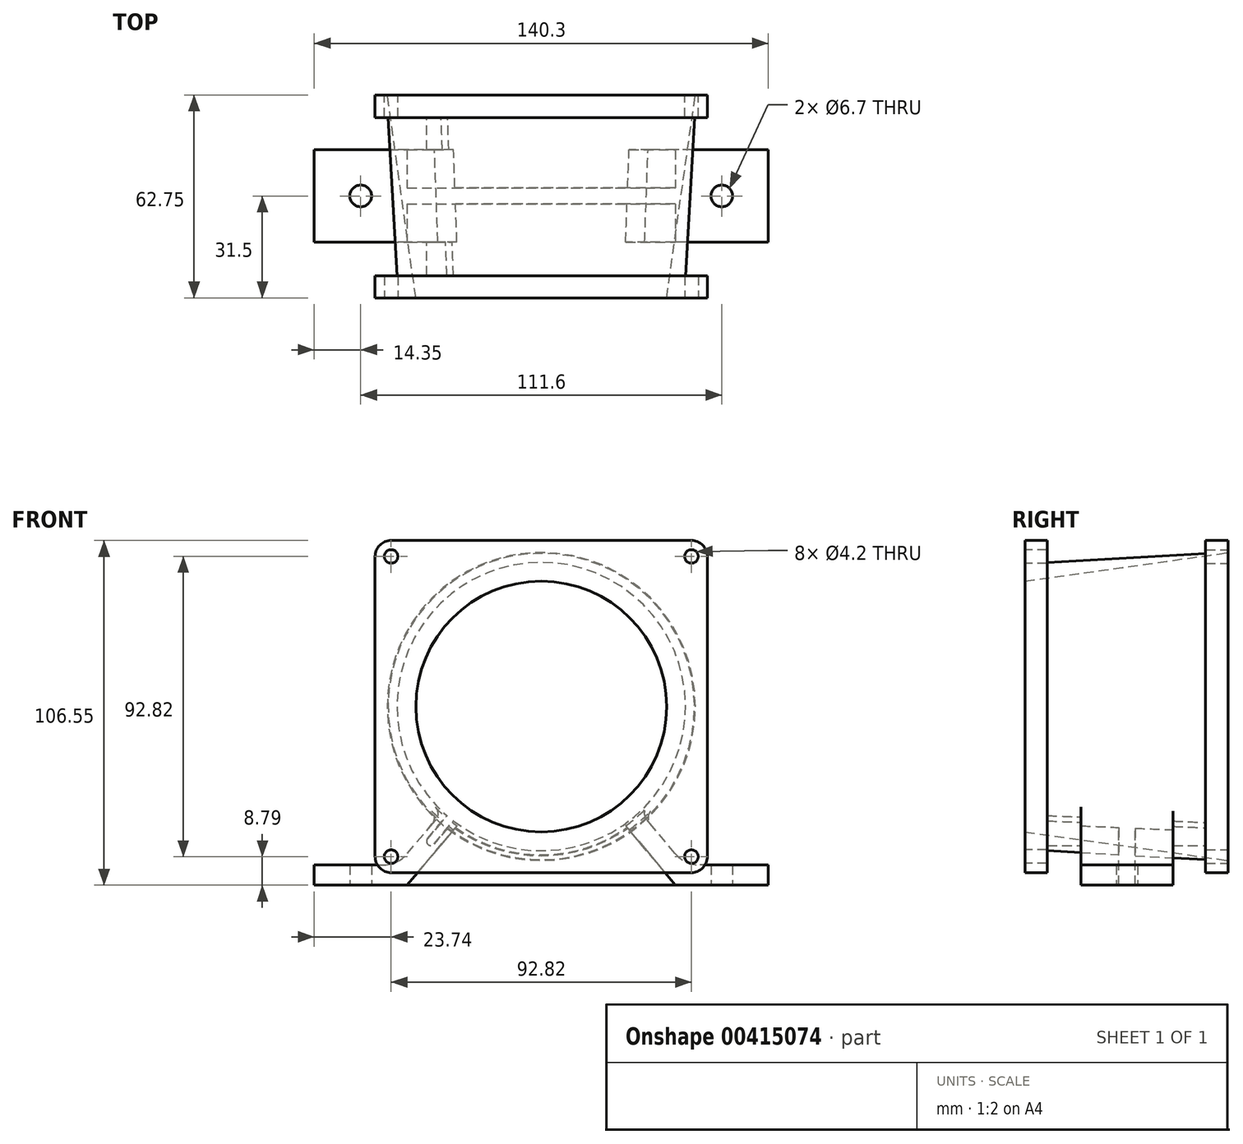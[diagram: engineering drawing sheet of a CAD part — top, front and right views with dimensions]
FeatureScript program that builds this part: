
annotation { "Feature Type Name" : "Feature", "Feature Type Description" : "" }
export const myFeature = defineFeature(function(context is Context, id is Id, definition is map)
    precondition{}
    {
        {
            var Q0;
            Q0=qCreatedBy(makeId("Front.planeOp"),FACE);
            var sketch = newSketch(context, id + "F0", { "sketchPlane" : qUnion([Q0])});
            skLineSegment(sketch, "E0.bottom", {"start": v(-51.35, 51.35) * mm, "end": v(51.35, 51.35) * mm});
            skLineSegment(sketch, "E0.top", {"start": v(-51.35, -51.35) * mm, "end": v(51.35, -51.35) * mm});
            skLineSegment(sketch, "E0.left", {"start": v(-51.35, 51.35) * mm, "end": v(-51.35, -51.35) * mm});
            skLineSegment(sketch, "E0.right", {"start": v(51.35, 51.35) * mm, "end": v(51.35, -51.35) * mm});
            skPoint(sketch, "E0.middle", {"position": v(0, 0) * mm});
            skCircle(sketch, "E1", {"center": v(46.4, 46.41) * mm, "radius": 2.1 * mm});
            skLineSegment(sketch, "E2", {"start": v(0, 51.35) * mm, "end": v(0, -51.35) * mm, "construction": true});
            skLineSegment(sketch, "E3", {"start": v(-51.35, 0) * mm, "end": v(51.35, 0) * mm, "construction": true});
            skCircle(sketch, "E4.MirrorC", {"center": v(-46.4, 46.41) * mm, "radius": 2.1 * mm});
            skCircle(sketch, "E5.MirrorC", {"center": v(-46.4, -46.41) * mm, "radius": 2.1 * mm});
            skCircle(sketch, "E6.MirrorC", {"center": v(46.4, -46.41) * mm, "radius": 2.1 * mm});
            skSolve(sketch);
        }
        {
            var Q0;
            Q0=makeQuery(id+"F0.imprint","IMPRINT",FACE,{"disambiguationData":[TD([[makeQuery(id+"F0.imprint","IMPRINT",EDGE,{"derivedFrom":sQuery(id+"F0.wireOp",EDGE,"E0.bottom")}),-1.0]])]});
            extrude(context, id + "F1", {"entities" : qUnion([Q0]), "oppositeDirection" : true, "depth" : 6.85 * mm});
        }
        {
            var Q0;
            Q0=makeQuery(id+"F1.opExtrude","SWEPT_EDGE",EDGE,{"disambiguationData":[OSD([sQuery(id+"F0.wireOp",EDGE,"E0.bottom"),sQuery(id+"F0.wireOp",EDGE,"E0.left")])]});
            var Q1;
            Q1=makeQuery(id+"F1.opExtrude","SWEPT_EDGE",EDGE,{"disambiguationData":[OSD([sQuery(id+"F0.wireOp",EDGE,"E0.bottom"),sQuery(id+"F0.wireOp",EDGE,"E0.right")])]});
            var Q2;
            Q2=makeQuery(id+"F1.opExtrude","SWEPT_EDGE",EDGE,{"disambiguationData":[OSD([sQuery(id+"F0.wireOp",EDGE,"E0.top"),sQuery(id+"F0.wireOp",EDGE,"E0.right")])]});
            var Q3;
            Q3=makeQuery(id+"F1.opExtrude","SWEPT_EDGE",EDGE,{"disambiguationData":[OSD([sQuery(id+"F0.wireOp",EDGE,"E0.top"),sQuery(id+"F0.wireOp",EDGE,"E0.left")])]});
            fillet(context, id + "F2", {"entities" : qUnion([Q0, Q1, Q2, Q3]), "radius" : 5 * mm, "tangentPropagation" : true, "allowEdgeOverflow" : false});
        }
        {
            var Q0;
            Q0=makeQuery(id+"F1.opExtrude","CAP_FACE",FACE,{"disambiguationData":[OSD([sQuery(id+"F0.wireOp",EDGE,"E0.bottom"),sQuery(id+"F0.wireOp",EDGE,"E0.top"),sQuery(id+"F0.wireOp",EDGE,"E0.left"),sQuery(id+"F0.wireOp",EDGE,"E0.right"),sQuery(id+"F0.wireOp",EDGE,"E1"),sQuery(id+"F0.wireOp",EDGE,"E4.MirrorC"),sQuery(id+"F0.wireOp",EDGE,"E5.MirrorC"),sQuery(id+"F0.wireOp",EDGE,"E6.MirrorC")])],"isStart":false});
            cPlane(context, id + "F3", {"entities" : qUnion([Q0]), "cplaneType" : CPlaneType.OFFSET, "offset" : 55.9 * mm, "width" : 150 * mm, "height" : 150 * mm});
        }
        {
            var Q0;
            Q0=qCreatedBy(id+"F3.planeOp",FACE);
            var sketch = newSketch(context, id + "F4", { "sketchPlane" : qUnion([Q0])});
            skLineSegment(sketch, "E7.bottom", {"start": v(-51.35, 51.35) * mm, "end": v(51.35, 51.35) * mm});
            skLineSegment(sketch, "E7.top", {"start": v(-51.35, -51.35) * mm, "end": v(51.35, -51.35) * mm});
            skLineSegment(sketch, "E7.left", {"start": v(-51.35, 51.35) * mm, "end": v(-51.35, -51.35) * mm});
            skLineSegment(sketch, "E7.right", {"start": v(51.35, 51.35) * mm, "end": v(51.35, -51.35) * mm});
            skPoint(sketch, "E7.middle", {"position": v(0, 0) * mm});
            skCircle(sketch, "E8.0", {"center": v(-46.4, 46.41) * mm, "radius": 2.1 * mm});
            skCircle(sketch, "E9.0", {"center": v(46.4, 46.41) * mm, "radius": 2.1 * mm});
            skCircle(sketch, "E10.0", {"center": v(46.4, -46.41) * mm, "radius": 2.1 * mm});
            skCircle(sketch, "E11.0", {"center": v(-46.4, -46.41) * mm, "radius": 2.1 * mm});
            skSolve(sketch);
        }
        {
            var Q0;
            Q0=makeQuery(id+"F4.imprint","IMPRINT",FACE,{"disambiguationData":[TD([[makeQuery(id+"F4.imprint","IMPRINT",EDGE,{"derivedFrom":sQuery(id+"F4.wireOp",EDGE,"E7.bottom")}),-1.0]])]});
            extrude(context, id + "F5", {"entities" : qUnion([Q0]), "oppositeDirection" : true, "depth" : 7 * mm});
        }
        {
            var Q0;
            Q0=makeQuery(id+"F5.opExtrude","SWEPT_EDGE",EDGE,{"disambiguationData":[OSD([sQuery(id+"F4.wireOp",EDGE,"E7.bottom"),sQuery(id+"F4.wireOp",EDGE,"E7.left")])]});
            var Q1;
            Q1=makeQuery(id+"F5.opExtrude","SWEPT_EDGE",EDGE,{"disambiguationData":[OSD([sQuery(id+"F4.wireOp",EDGE,"E7.bottom"),sQuery(id+"F4.wireOp",EDGE,"E7.right")])]});
            var Q2;
            Q2=makeQuery(id+"F5.opExtrude","SWEPT_EDGE",EDGE,{"disambiguationData":[OSD([sQuery(id+"F4.wireOp",EDGE,"E7.top"),sQuery(id+"F4.wireOp",EDGE,"E7.right")])]});
            var Q3;
            Q3=makeQuery(id+"F5.opExtrude","SWEPT_EDGE",EDGE,{"disambiguationData":[OSD([sQuery(id+"F4.wireOp",EDGE,"E7.top"),sQuery(id+"F4.wireOp",EDGE,"E7.left")])]});
            fillet(context, id + "F6", {"entities" : qUnion([Q0, Q1, Q2, Q3]), "radius" : 5 * mm, "tangentPropagation" : true, "allowEdgeOverflow" : false});
        }
        {
            var Q0;
            Q0=makeQuery(id+"F1.opExtrude","CAP_FACE",FACE,{"disambiguationData":[OSD([sQuery(id+"F0.wireOp",EDGE,"E0.bottom"),sQuery(id+"F0.wireOp",EDGE,"E0.top"),sQuery(id+"F0.wireOp",EDGE,"E0.left"),sQuery(id+"F0.wireOp",EDGE,"E0.right"),sQuery(id+"F0.wireOp",EDGE,"E1"),sQuery(id+"F0.wireOp",EDGE,"E4.MirrorC"),sQuery(id+"F0.wireOp",EDGE,"E5.MirrorC"),sQuery(id+"F0.wireOp",EDGE,"E6.MirrorC")])],"isStart":true});
            var sketch = newSketch(context, id + "F7", { "sketchPlane" : qUnion([Q0])});
            skCircle(sketch, "E12.0", {"center": v(0, 0) * mm, "radius": 44.18 * mm});
            skSolve(sketch);
        }
        {
            var Q0;
            Q0=makeQuery(id+"F5.opExtrude","CAP_FACE",FACE,{"disambiguationData":[OSD([sQuery(id+"F4.wireOp",EDGE,"E7.bottom"),sQuery(id+"F4.wireOp",EDGE,"E7.top"),sQuery(id+"F4.wireOp",EDGE,"E7.left"),sQuery(id+"F4.wireOp",EDGE,"E7.right"),sQuery(id+"F4.wireOp",EDGE,"E8.0"),sQuery(id+"F4.wireOp",EDGE,"E9.0"),sQuery(id+"F4.wireOp",EDGE,"E10.0"),sQuery(id+"F4.wireOp",EDGE,"E11.0")])],"isStart":true});
            var sketch = newSketch(context, id + "F8", { "sketchPlane" : qUnion([Q0])});
            skCircle(sketch, "E13.0", {"center": v(0, 0) * mm, "radius": 47.75 * mm});
            skSolve(sketch);
        }
        {
            var Q0;
            Q0=makeQuery(id+"F7.imprint","IMPRINT",FACE,{"disambiguationData":[TD([[makeQuery(id+"F7.imprint","IMPRINT",EDGE,{"derivedFrom":sQuery(id+"F7.wireOp",EDGE,"E12.0")}),1.0]])]});
            var Q1;
            Q1=makeQuery(id+"F8.imprint","IMPRINT",FACE,{"disambiguationData":[TD([[makeQuery(id+"F8.imprint","IMPRINT",EDGE,{"derivedFrom":sQuery(id+"F8.wireOp",EDGE,"E13.0")}),1.0]])]});
            loft(context, id + "F9", {"operationType" : NewBodyOperationType.ADD, "sheetProfilesArray" : [{ "sheetProfileEntities" : qUnion([Q0]) }, { "sheetProfileEntities" : qUnion([Q1]) }]});
        }
        {
            var Q0;
            Q0=makeQuery(id+"F7.imprint","IMPRINT",FACE,{"disambiguationData":[TD([[makeQuery(id+"F7.imprint","IMPRINT",EDGE,{"derivedFrom":sQuery(id+"F7.wireOp",EDGE,"E12.0")}),1.0]])]});
            var sketch = newSketch(context, id + "F10", { "sketchPlane" : qUnion([Q0])});
            skCircle(sketch, "E14.0", {"center": v(0, 0) * mm, "radius": 44.18 * mm});
            skCircle(sketch, "E15.0", {"center": v(0, 0) * mm, "radius": 38.75 * mm});
            skSolve(sketch);
        }
        {
            var Q0;
            Q0=makeQuery(id+"F8.imprint","IMPRINT",FACE,{"disambiguationData":[TD([[makeQuery(id+"F8.imprint","IMPRINT",EDGE,{"derivedFrom":sQuery(id+"F8.wireOp",EDGE,"E13.0")}),1.0]])]});
            var sketch = newSketch(context, id + "F11", { "sketchPlane" : qUnion([Q0])});
            skCircle(sketch, "E16.0", {"center": v(0, 0) * mm, "radius": 47.75 * mm});
            skCircle(sketch, "E17.0", {"center": v(0, 0) * mm, "radius": 47.6 * mm});
            skSolve(sketch);
        }
        {
            var Q0;
            Q0=makeQuery(id+"F1.opExtrude","CAP_FACE",FACE,{"disambiguationData":[OSD([sQuery(id+"F0.wireOp",EDGE,"E0.bottom"),sQuery(id+"F0.wireOp",EDGE,"E0.top"),sQuery(id+"F0.wireOp",EDGE,"E0.left"),sQuery(id+"F0.wireOp",EDGE,"E0.right"),sQuery(id+"F0.wireOp",EDGE,"E1"),sQuery(id+"F0.wireOp",EDGE,"E4.MirrorC"),sQuery(id+"F0.wireOp",EDGE,"E5.MirrorC"),sQuery(id+"F0.wireOp",EDGE,"E6.MirrorC")])],"isStart":false});
            cPlane(context, id + "F12", {"entities" : qUnion([Q0]), "cplaneType" : CPlaneType.OFFSET, "offset" : 10.4 * mm, "width" : 150 * mm, "height" : 150 * mm});
        }
        {
            var Q0;
            Q0=qCreatedBy(id+"F12.planeOp",FACE);
            var sketch = newSketch(context, id + "F13", { "sketchPlane" : qUnion([Q0])});
            skLineSegment(sketch, "E18.0", {"start": v(46.35, -51.35) * mm, "end": v(-46.35, -51.35) * mm, "construction": true});
            skLineSegment(sketch, "E19.0", {"start": v(34.1, -55.2) * mm, "end": v(-47.5, -55.2) * mm, "construction": true});
            skLineSegment(sketch, "E20.0", {"start": v(-51.35, 46.35) * mm, "end": v(-51.35, -46.35) * mm, "construction": true});
            skLineSegment(sketch, "E21", {"start": v(-51.35, -46.35) * mm, "end": v(-51.35, -55.2) * mm, "construction": true});
            skLineSegment(sketch, "E22", {"start": v(-51.35, -55.2) * mm, "end": v(-47.5, -55.2) * mm, "construction": true});
            skLineSegment(sketch, "E23.0", {"start": v(-70.15, -40.95) * mm, "end": v(-70.15, -55.2) * mm, "construction": true});
            skLineSegment(sketch, "E24", {"start": v(-70.15, -55.2) * mm, "end": v(-41.45, -55.2) * mm});
            skLineSegment(sketch, "E25", {"start": v(-70.15, -55.2) * mm, "end": v(-70.15, -49) * mm});
            skLineSegment(sketch, "E26", {"start": v(-70.15, -49) * mm, "end": v(-44.34, -49) * mm});
            skLineSegment(sketch, "E27", {"start": v(-44.34, -49) * mm, "end": v(-23.82, -24.54) * mm});
            skLineSegment(sketch, "E28", {"start": v(-23.82, -24.54) * mm, "end": v(-19.07, -28.52) * mm});
            skLineSegment(sketch, "E29", {"start": v(-19.07, -28.52) * mm, "end": v(-41.45, -55.2) * mm});
            skLineSegment(sketch, "E30.MirrorCS", {"start": v(23.82, -24.54) * mm, "end": v(19.07, -28.52) * mm});
            skLineSegment(sketch, "E31.MirrorCS", {"start": v(44.34, -49) * mm, "end": v(23.82, -24.54) * mm});
            skLineSegment(sketch, "E32.MirrorCS", {"start": v(19.07, -28.52) * mm, "end": v(41.45, -55.2) * mm});
            skLineSegment(sketch, "E33.MirrorCS", {"start": v(70.15, -55.2) * mm, "end": v(41.45, -55.2) * mm});
            skLineSegment(sketch, "E34.MirrorCS", {"start": v(70.15, -49) * mm, "end": v(44.34, -49) * mm});
            skLineSegment(sketch, "E35.MirrorCS", {"start": v(70.15, -55.2) * mm, "end": v(70.15, -49) * mm});
            skSolve(sketch);
        }
        {
            var Q0;
            Q0=makeQuery(id+"F13.imprint","IMPRINT",FACE,{"disambiguationData":[TD([[makeQuery(id+"F13.imprint","IMPRINT",EDGE,{"derivedFrom":sQuery(id+"F13.wireOp",EDGE,"E30.MirrorCS")}),1.0]])]});
            var Q1;
            Q1=makeQuery(id+"F13.imprint","IMPRINT",FACE,{"disambiguationData":[TD([[makeQuery(id+"F13.imprint","IMPRINT",EDGE,{"derivedFrom":sQuery(id+"F13.wireOp",EDGE,"E24")}),1.0]])]});
            extrude(context, id + "F14", {"entities" : qUnion([Q0, Q1]), "operationType" : NewBodyOperationType.ADD, "depth" : 28.5 * mm});
        }
        {
            var Q0;
            Q0=makeQuery(id+"F14.opExtrude","CAP_FACE",FACE,{"disambiguationData":[OSD([sQuery(id+"F13.wireOp",EDGE,"E30.MirrorCS"),sQuery(id+"F13.wireOp",EDGE,"E31.MirrorCS"),sQuery(id+"F13.wireOp",EDGE,"E32.MirrorCS"),sQuery(id+"F13.wireOp",EDGE,"E33.MirrorCS"),sQuery(id+"F13.wireOp",EDGE,"E34.MirrorCS"),sQuery(id+"F13.wireOp",EDGE,"E35.MirrorCS")])],"isStart":true});
            var sketch = newSketch(context, id + "F15", { "sketchPlane" : qUnion([Q0])});
            skLineSegment(sketch, "E36.0", {"start": v(-44.34, -49) * mm, "end": v(-30.88, -32.96) * mm, "construction": true});
            skLineSegment(sketch, "E37.0", {"start": v(-26.07, -36.87) * mm, "end": v(-41.45, -55.2) * mm, "construction": true});
            skLineSegment(sketch, "E38", {"start": v(-37.6, -40.98) * mm, "end": v(-32.86, -44.96) * mm, "construction": true});
            skLineSegment(sketch, "E39", {"start": v(-28.54, -35) * mm, "end": v(-34.14, -41.66) * mm, "construction": true});
            skArc(sketch, "E40", {"start": v(-35.13, -40.83) * mm, "mid": v(-34.97, -42.66) * mm, "end": v(-33.14, -42.5) * mm});
            skLineSegment(sketch, "E41", {"start": v(-35.13, -40.83) * mm, "end": v(-24.59, -28.26) * mm});
            skLineSegment(sketch, "E42", {"start": v(-33.14, -42.5) * mm, "end": v(-22.6, -29.93) * mm});
            skLineSegment(sketch, "E43", {"start": v(-22.6, -29.93) * mm, "end": v(-24.59, -28.26) * mm});
            skArc(sketch, "E44.MirrorCS", {"start": v(35.13, -40.83) * mm, "mid": v(34.97, -42.66) * mm, "end": v(33.14, -42.5) * mm});
            skLineSegment(sketch, "E45.MirrorCS", {"start": v(22.6, -29.93) * mm, "end": v(24.59, -28.26) * mm});
            skLineSegment(sketch, "E46.MirrorCS", {"start": v(33.14, -42.5) * mm, "end": v(22.6, -29.93) * mm});
            skLineSegment(sketch, "E47.MirrorCS", {"start": v(35.13, -40.83) * mm, "end": v(24.59, -28.26) * mm});
            skSolve(sketch);
        }
        {
            var Q0;
            {var subQ0=sQuery(id+"F15.wireOp",EDGE,"E40");Q0=makeQuery(id+"F15.imprint","IMPRINT",FACE,{"disambiguationData":[TD([[makeQuery(id+"F15.imprint","IMPRINT",EDGE,{"derivedFrom":subQ0}),1.0]])]});}
            var Q1;
            {var subQ0=sQuery(id+"F15.wireOp",EDGE,"E43");Q1=makeQuery(id+"F15.imprint","IMPRINT",FACE,{"disambiguationData":[TD([[makeQuery(id+"F15.imprint","IMPRINT",EDGE,{"derivedFrom":subQ0}),1.0]])]});}
            var Q2;
            Q2=makeQuery(id+"F15.imprint","IMPRINT",FACE,{"disambiguationData":[TD([[makeQuery(id+"F15.imprint","IMPRINT",EDGE,{"derivedFrom":sQuery(id+"F15.wireOp",EDGE,"E44.MirrorCS")}),-1.0]])]});
            var Q3;
            Q3=makeQuery(id+"F1.opExtrude","CAP_FACE",FACE,{"disambiguationData":[OSD([sQuery(id+"F0.wireOp",EDGE,"E0.bottom"),sQuery(id+"F0.wireOp",EDGE,"E0.top"),sQuery(id+"F0.wireOp",EDGE,"E0.left"),sQuery(id+"F0.wireOp",EDGE,"E0.right"),sQuery(id+"F0.wireOp",EDGE,"E1"),sQuery(id+"F0.wireOp",EDGE,"E4.MirrorC"),sQuery(id+"F0.wireOp",EDGE,"E5.MirrorC"),sQuery(id+"F0.wireOp",EDGE,"E6.MirrorC")])],"isStart":false});
            var Q4;
            Q4=makeQuery(id+"F5.opExtrude","CAP_FACE",FACE,{"disambiguationData":[OSD([sQuery(id+"F4.wireOp",EDGE,"E7.bottom"),sQuery(id+"F4.wireOp",EDGE,"E7.top"),sQuery(id+"F4.wireOp",EDGE,"E7.left"),sQuery(id+"F4.wireOp",EDGE,"E7.right"),sQuery(id+"F4.wireOp",EDGE,"E8.0"),sQuery(id+"F4.wireOp",EDGE,"E9.0"),sQuery(id+"F4.wireOp",EDGE,"E10.0"),sQuery(id+"F4.wireOp",EDGE,"E11.0")])],"isStart":false});
            extrude(context, id + "F16", {"entities" : qUnion([Q0, Q1, Q2]), "operationType" : NewBodyOperationType.ADD, "endBound" : BoundingType.UP_TO_SURFACE, "endBoundEntityFace" : qUnion([Q3]), "depth" : 25 * mm, "hasSecondDirection" : true, "secondDirectionBound" : SecondDirectionBoundingType.UP_TO_SURFACE, "secondDirectionOppositeDirection" : true, "secondDirectionBoundEntityFace" : qUnion([Q4]), "secondDirectionDepth" : 25 * mm});
        }
        {
            var Q1;
            Q1=makeQuery(id+"F10.imprint","IMPRINT",FACE,{"disambiguationData":[TD([[makeQuery(id+"F10.imprint","IMPRINT",EDGE,{"derivedFrom":sQuery(id+"F10.wireOp",EDGE,"E15.0")}),1.0]])]});
            var Q2;
            Q2=makeQuery(id+"F11.imprint","IMPRINT",FACE,{"disambiguationData":[TD([[makeQuery(id+"F11.imprint","IMPRINT",EDGE,{"derivedFrom":sQuery(id+"F11.wireOp",EDGE,"E17.0")}),1.0]])]});
            loft(context, id + "F17", {"operationType" : NewBodyOperationType.REMOVE, "sheetProfilesArray" : [{ "sheetProfileEntities" : qUnion([Q1]) }, { "sheetProfileEntities" : qUnion([Q2]) }]});
        }
        {
            var Q0;
            Q0=makeQuery(id+"F14.opExtrude","SWEPT_FACE",FACE,{"disambiguationData":[OSD([sQuery(id+"F13.wireOp",EDGE,"E33.MirrorCS")])]});
            var sketch = newSketch(context, id + "F18", { "sketchPlane" : qUnion([Q0])});
            skLineSegment(sketch, "E48", {"start": v(-41.45, -31.5) * mm, "end": v(30.35, -31.5) * mm, "construction": true});
            skLineSegment(sketch, "E49.0", {"start": v(-41.45, -34) * mm, "end": v(30.35, -34) * mm});
            skLineSegment(sketch, "E50.0", {"start": v(-41.45, -29) * mm, "end": v(30.35, -29) * mm});
            skLineSegment(sketch, "E51", {"start": v(-41.45, -29) * mm, "end": v(-41.45, -34) * mm});
            skLineSegment(sketch, "E52.0", {"start": v(41.45, -34) * mm, "end": v(41.45, -29) * mm});
            skLineSegment(sketch, "E53", {"start": v(30.35, -29) * mm, "end": v(41.45, -29) * mm});
            skLineSegment(sketch, "E54", {"start": v(30.35, -34) * mm, "end": v(41.45, -34) * mm});
            skSolve(sketch);
        }
        {
            var Q0;
            Q0=makeQuery(id+"F18.imprint","IMPRINT",FACE,{"disambiguationData":[TD([[makeQuery(id+"F18.imprint","IMPRINT",EDGE,{"derivedFrom":sQuery(id+"F18.wireOp",EDGE,"E49.0")}),1.0]])]});
            var Q1;
            {var subQ0=sQuery(id+"F13.wireOp",EDGE,"E29");Q1=makeQuery(id+"F16.boolean.opBoolean","SPLIT",FACE,{"disambiguationData":[TD([makeQuery(id+"F14.opExtrude","SWEPT_FACE",FACE,{"disambiguationData":[OSD([subQ0])]})])],"derivedFrom":makeQuery(id+"F9.opLoft","SWEPT_FACE",FACE,{"disambiguationData":[OSD([sQuery(id+"F7.wireOp",EDGE,"E12.0"),sQuery(id+"F8.wireOp",EDGE,"E13.0")])]})});}
            var Q2;
            Q2=makeQuery(id+"F1.opExtrude","SWEPT_BODY",BODY,{"disambiguationData":[OSD([sQuery(id+"F0.wireOp",EDGE,"E0.bottom"),sQuery(id+"F0.wireOp",EDGE,"E0.top"),sQuery(id+"F0.wireOp",EDGE,"E0.left"),sQuery(id+"F0.wireOp",EDGE,"E0.right"),sQuery(id+"F0.wireOp",EDGE,"E1"),sQuery(id+"F0.wireOp",EDGE,"E4.MirrorC"),sQuery(id+"F0.wireOp",EDGE,"E5.MirrorC"),sQuery(id+"F0.wireOp",EDGE,"E6.MirrorC")])]});
            extrude(context, id + "F19", {"entities" : qUnion([Q0]), "operationType" : NewBodyOperationType.ADD, "endBound" : BoundingType.UP_TO_BODY, "oppositeDirection" : true, "endBoundEntityFace" : qUnion([Q1]), "endBoundEntityBody" : qUnion([Q2]), "depth" : 25 * mm});
        }
        {
            var Q0;
            Q0=makeQuery(id+"F19.boolean.opBoolean","MERGE",FACE,{"derivedFrom":[makeQuery(id+"F14.opExtrude","SWEPT_FACE",FACE,{"disambiguationData":[OSD([sQuery(id+"F13.wireOp",EDGE,"E24")])]}),makeQuery(id+"F14.opExtrude","SWEPT_FACE",FACE,{"disambiguationData":[OSD([sQuery(id+"F13.wireOp",EDGE,"E33.MirrorCS")])]}),makeQuery(id+"F19.opExtrude","CAP_FACE",FACE,{"disambiguationData":[OSD([sQuery(id+"F18.wireOp",EDGE,"E49.0"),sQuery(id+"F18.wireOp",EDGE,"E50.0"),sQuery(id+"F18.wireOp",EDGE,"E51"),sQuery(id+"F18.wireOp",EDGE,"VDJPXkP9-P6EK-BHMD-2L8I-CgkqJzvVx65P")])],"isStart":true})]});
            var sketch = newSketch(context, id + "F20", { "sketchPlane" : qUnion([Q0])});
            skLineSegment(sketch, "E55.0", {"start": v(-70.15, -45.75) * mm, "end": v(-70.15, -17.25) * mm, "construction": true});
            skLineSegment(sketch, "E56.0", {"start": v(-70.15, -17.25) * mm, "end": v(-41.45, -17.25) * mm, "construction": true});
            skLineSegment(sketch, "E57.0", {"start": v(70.15, -17.25) * mm, "end": v(41.45, -17.25) * mm, "construction": true});
            skLineSegment(sketch, "E58.0", {"start": v(70.15, -45.75) * mm, "end": v(70.15, -17.25) * mm, "construction": true});
            skPoint(sketch, "E59", {"position": v(-55.8, -31.5) * mm});
            skPoint(sketch, "E59.positionSnap0", {"position": v(-55.8, -17.25) * mm});
            skPoint(sketch, "E59.positionSnap1", {"position": v(-70.15, -31.5) * mm});
            skPoint(sketch, "E60", {"position": v(55.8, -31.5) * mm});
            skPoint(sketch, "E60.positionSnap0", {"position": v(55.8, -17.25) * mm});
            skPoint(sketch, "E60.positionSnap1", {"position": v(70.15, -31.5) * mm});
            skCircle(sketch, "E61", {"center": v(-55.8, -31.5) * mm, "radius": 3.35 * mm});
            skCircle(sketch, "E62", {"center": v(55.8, -31.5) * mm, "radius": 3.35 * mm});
            skSolve(sketch);
        }
        {
            var Q0;
            Q0=makeQuery(id+"F20.imprint","IMPRINT",FACE,{"disambiguationData":[TD([[makeQuery(id+"F20.imprint","IMPRINT",EDGE,{"derivedFrom":sQuery(id+"F20.wireOp",EDGE,"E62")}),1.0]])]});
            var Q1;
            Q1=makeQuery(id+"F20.imprint","IMPRINT",FACE,{"disambiguationData":[TD([[makeQuery(id+"F20.imprint","IMPRINT",EDGE,{"derivedFrom":sQuery(id+"F20.wireOp",EDGE,"E61")}),1.0]])]});
            var Q2;
            Q2=makeQuery(id+"F14.opExtrude","SWEPT_FACE",FACE,{"disambiguationData":[OSD([sQuery(id+"F13.wireOp",EDGE,"E34.MirrorCS")])]});
            extrude(context, id + "F21", {"entities" : qUnion([Q0, Q1]), "operationType" : NewBodyOperationType.REMOVE, "endBound" : BoundingType.UP_TO_SURFACE, "oppositeDirection" : true, "endBoundEntityFace" : qUnion([Q2]), "depth" : 25 * mm});
        }
        {
            var Q0;
            {var subQ0=sQuery(id+"F13.wireOp",EDGE,"E29");Q0=makeQuery(id+"F19.opExtrude","TWEAK_EDGE",EDGE,{"derivedFrom":[makeQuery(id+"F16.boolean.opBoolean","SPLIT",FACE,{"disambiguationData":[TD([makeQuery(id+"F14.opExtrude","SWEPT_FACE",FACE,{"disambiguationData":[OSD([subQ0])]})])],"derivedFrom":makeQuery(id+"F9.opLoft","SWEPT_FACE",FACE,{"disambiguationData":[OSD([sQuery(id+"F7.wireOp",EDGE,"E12.0"),sQuery(id+"F8.wireOp",EDGE,"E13.0")])]})}),makeQuery(id+"F18.imprint","IMPRINT",EDGE,{"derivedFrom":sQuery(id+"F18.wireOp",EDGE,"E50.0")})]});}
            var Q1;
            Q1=makeQuery(id+"F19.opExtrude","TWEAK_EDGE",EDGE,{"derivedFrom":[makeQuery(id+"F14.opExtrude","SWEPT_FACE",FACE,{"disambiguationData":[OSD([sQuery(id+"F13.wireOp",EDGE,"E32.MirrorCS")])]}),makeQuery(id+"F18.imprint","IMPRINT",EDGE,{"derivedFrom":sQuery(id+"F18.wireOp",EDGE,"E50.0")})]});
            var Q2;
            Q2=makeQuery(id+"F19.opExtrude","TWEAK_EDGE",EDGE,{"derivedFrom":[makeQuery(id+"F14.opExtrude","SWEPT_FACE",FACE,{"disambiguationData":[OSD([sQuery(id+"F13.wireOp",EDGE,"E29")])]}),makeQuery(id+"F18.imprint","IMPRINT",EDGE,{"derivedFrom":sQuery(id+"F18.wireOp",EDGE,"E50.0")})]});
            var Q3;
            Q3=makeQuery(id+"F19.opExtrude","TWEAK_EDGE",EDGE,{"derivedFrom":[makeQuery(id+"F14.opExtrude","SWEPT_FACE",FACE,{"disambiguationData":[OSD([sQuery(id+"F13.wireOp",EDGE,"E32.MirrorCS")])]}),makeQuery(id+"F18.imprint","IMPRINT",EDGE,{"derivedFrom":sQuery(id+"F18.wireOp",EDGE,"E49.0")})]});
            var Q4;
            {var subQ0=sQuery(id+"F13.wireOp",EDGE,"E29");Q4=makeQuery(id+"F19.opExtrude","TWEAK_EDGE",EDGE,{"derivedFrom":[makeQuery(id+"F16.boolean.opBoolean","SPLIT",FACE,{"disambiguationData":[TD([makeQuery(id+"F14.opExtrude","SWEPT_FACE",FACE,{"disambiguationData":[OSD([subQ0])]})])],"derivedFrom":makeQuery(id+"F9.opLoft","SWEPT_FACE",FACE,{"disambiguationData":[OSD([sQuery(id+"F7.wireOp",EDGE,"E12.0"),sQuery(id+"F8.wireOp",EDGE,"E13.0")])]})}),makeQuery(id+"F18.imprint","IMPRINT",EDGE,{"derivedFrom":sQuery(id+"F18.wireOp",EDGE,"E49.0")})]});}
            var Q5;
            Q5=makeQuery(id+"F19.opExtrude","TWEAK_EDGE",EDGE,{"derivedFrom":[makeQuery(id+"F14.opExtrude","SWEPT_FACE",FACE,{"disambiguationData":[OSD([sQuery(id+"F13.wireOp",EDGE,"E29")])]}),makeQuery(id+"F18.imprint","IMPRINT",EDGE,{"derivedFrom":sQuery(id+"F18.wireOp",EDGE,"E49.0")})]});
            var Q6;
            Q6=makeQuery(id+"F14.boolean.opBoolean","INTERSECT",EDGE,{"derivedFrom":[makeQuery(id+"F9.opLoft","SWEPT_FACE",FACE,{"disambiguationData":[OSD([sQuery(id+"F7.wireOp",EDGE,"E12.0"),sQuery(id+"F8.wireOp",EDGE,"E13.0")])]}),makeQuery(id+"F14.opExtrude","SWEPT_FACE",FACE,{"disambiguationData":[OSD([sQuery(id+"F13.wireOp",EDGE,"E31.MirrorCS")])]})]});
            var Q7;
            Q7=makeQuery(id+"F14.boolean.opBoolean","INTERSECT",EDGE,{"derivedFrom":[makeQuery(id+"F9.opLoft","SWEPT_FACE",FACE,{"disambiguationData":[OSD([sQuery(id+"F7.wireOp",EDGE,"E12.0"),sQuery(id+"F8.wireOp",EDGE,"E13.0")])]}),makeQuery(id+"F14.opExtrude","SWEPT_FACE",FACE,{"disambiguationData":[OSD([sQuery(id+"F13.wireOp",EDGE,"E27")])]})]});
            fillet(context, id + "F22", {"entities" : qUnion([Q0, Q1, Q2, Q3, Q4, Q5, Q6, Q7]), "radius" : 3 * mm, "tangentPropagation" : true, "allowEdgeOverflow" : false});
        }
        {
            var Q0;
            Q0=makeQuery(id+"F14.opExtrude","SWEPT_EDGE",EDGE,{"disambiguationData":[OSD([sQuery(id+"F13.wireOp",EDGE,"E26"),sQuery(id+"F13.wireOp",EDGE,"E27")])]});
            var Q1;
            Q1=makeQuery(id+"F14.opExtrude","SWEPT_EDGE",EDGE,{"disambiguationData":[OSD([sQuery(id+"F13.wireOp",EDGE,"E31.MirrorCS"),sQuery(id+"F13.wireOp",EDGE,"E34.MirrorCS")])]});
            fillet(context, id + "F23", {"entities" : qUnion([Q0, Q1]), "radius" : 10 * mm, "tangentPropagation" : true, "allowEdgeOverflow" : false});
        }
    });
